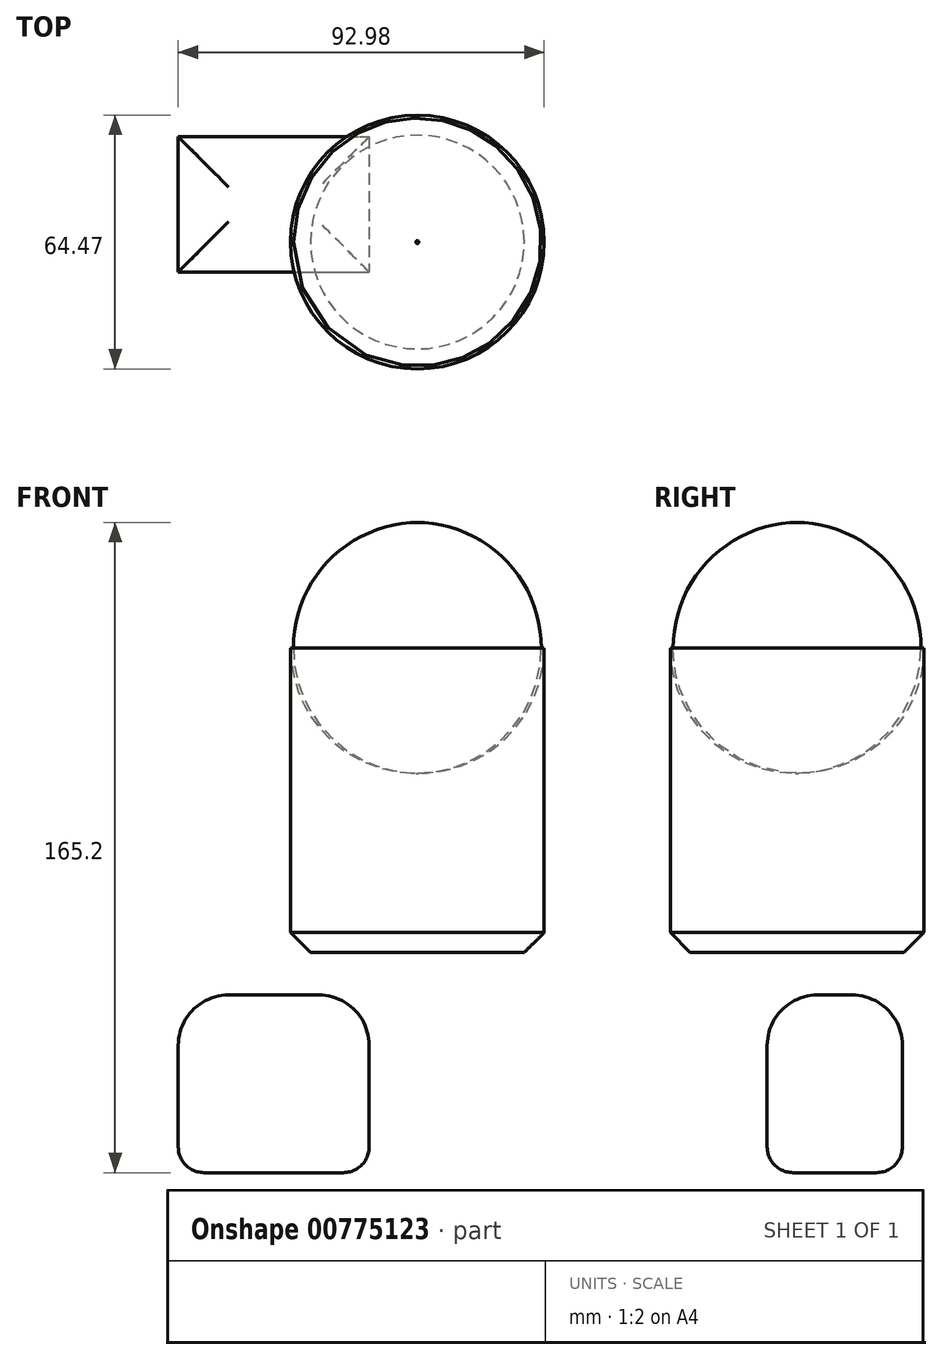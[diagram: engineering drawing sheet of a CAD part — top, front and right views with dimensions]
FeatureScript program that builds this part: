
annotation { "Feature Type Name" : "Feature", "Feature Type Description" : "" }
export const myFeature = defineFeature(function(context is Context, id is Id, definition is map)
    precondition{}
    {
        {
            var Q0;
            Q0=qCreatedBy(makeId("Top.planeOp"),FACE);
            var sketch = newSketch(context, id + "F0", { "sketchPlane" : qUnion([Q0])});
            skCircle(sketch, "E0", {"center": v(0, 7.6) * mm, "radius": 32.23 * mm});
            skSolve(sketch);
        }
        {
            var Q0;
            Q0 = qSketchRegion(id + "F0", true);
            extrude(context, id + "F1", {"entities" : qUnion([Q0]), "depth" : 109.26 * mm, "offsetDistance" : 25.4 * mm});
        }
        {
            var Q0;
            Q0=qCreatedBy(makeId("Front.planeOp"),FACE);
            var sketch = newSketch(context, id + "F2", { "sketchPlane" : qUnion([Q0])});
            skLineSegment(sketch, "E1.bottom", {"start": v(-60.75, -10.78) * mm, "end": v(-12.24, -10.78) * mm});
            skLineSegment(sketch, "E1.top", {"start": v(-60.75, -55.94) * mm, "end": v(-12.24, -55.94) * mm});
            skLineSegment(sketch, "E1.left", {"start": v(-60.75, -10.78) * mm, "end": v(-60.75, -55.94) * mm});
            skLineSegment(sketch, "E1.right", {"start": v(-12.24, -10.78) * mm, "end": v(-12.24, -55.94) * mm});
            skSolve(sketch);
        }
        {
            var Q0;
            Q0=makeQuery(id+"F2.imprint","IMPRINT",FACE,{"disambiguationData":[TD([[makeQuery(id+"F2.imprint","IMPRINT",EDGE,{"derivedFrom":sQuery(id+"F2.wireOp",EDGE,"E1.bottom")}),-1.0]])]});
            extrude(context, id + "F3", {"entities" : qUnion([Q0]), "oppositeDirection" : true, "depth" : 34.36 * mm, "offsetDistance" : 25.4 * mm});
        }
        {
            var Q0;
            Q0=makeQuery(id+"F3.opExtrude","SWEPT_FACE",FACE,{"disambiguationData":[OSD([sQuery(id+"F2.wireOp",EDGE,"E1.top")])]});
            fillet(context, id + "F4", {"entities" : qUnion([Q0]), "radius" : 6.55 * mm, "tangentPropagation" : true, "allowEdgeOverflow" : false});
        }
        {
            var Q0;
            Q0=makeQuery(id+"F3.opExtrude","SWEPT_FACE",FACE,{"disambiguationData":[OSD([sQuery(id+"F2.wireOp",EDGE,"E1.bottom")])]});
            fillet(context, id + "F5", {"entities" : qUnion([Q0]), "radius" : 12.79 * mm, "tangentPropagation" : true, "allowEdgeOverflow" : false});
        }
        {
            var Q0;
            Q0=makeQuery(id+"F1.opExtrude","CAP_FACE",FACE,{"disambiguationData":[OSD([sQuery(id+"F0.wireOp",EDGE,"E0")])],"isStart":false});
            fillet(context, id + "F6", {"entities" : qUnion([Q0]), "radius" : 31.86 * mm, "tangentPropagation" : true, "allowEdgeOverflow" : false});
        }
        {
            var Q0;
            Q0=makeQuery(id+"F1.opExtrude","CAP_FACE",FACE,{"disambiguationData":[OSD([sQuery(id+"F0.wireOp",EDGE,"E0")])],"isStart":true});
            chamfer(context, id + "F7", {"entities" : qUnion([Q0]), "width" : 5.08 * mm, "tangentPropagation" : true});
        }
    });
